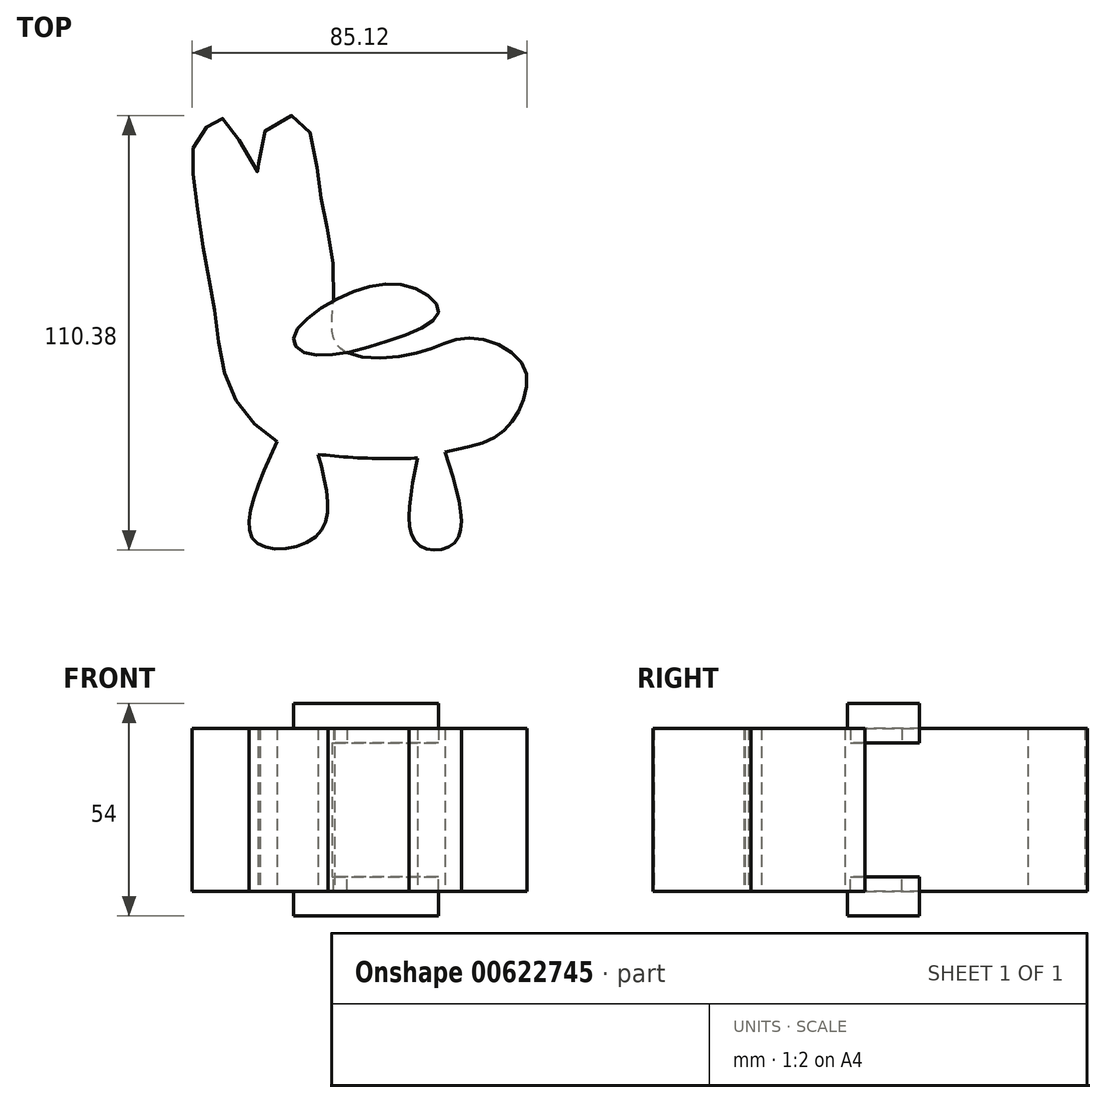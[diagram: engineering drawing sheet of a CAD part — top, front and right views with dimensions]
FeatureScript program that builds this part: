
annotation { "Feature Type Name" : "Feature", "Feature Type Description" : "" }
export const myFeature = defineFeature(function(context is Context, id is Id, definition is map)
    precondition{}
    {
        {
            var Q0;
            Q0=qCreatedBy(makeId("Top.planeOp"),FACE);
            var sketch = newSketch(context, id + "F0", { "sketchPlane" : qUnion([Q0])});
            skFitSpline(sketch, "E0", {"points": [v(13.16, -18.78) * mm, v(0, -22.63) * mm, v(-19.97, -21.15) * mm, v(-21.15, -6.36) * mm, v(-23.52, 11.68) * mm, v(-25.59, 24.4) * mm, v(-30.32, 37.42) * mm, v(-40.08, 31.2) * mm, v(-40.08, 22.63) * mm, v(-47.77, 35.35) * mm, v(-50.73, 36.83) * mm, v(-56.35, 31.2) * mm, v(-56.94, 22.04) * mm, v(-54.28, 2.81) * mm, v(-51.62, -11.1) * mm, v(-49.55, -25.59) * mm, v(-44.52, -37.12) * mm, v(-35.64, -45.1) * mm, v(-25.3, -48.36) * mm, v(0, -49.25) * mm, v(6.95, -47.77) * mm, v(18.78, -44.52) * mm, v(25.88, -36.83) * mm, v(26.77, -25.59) * mm, v(13.16, -18.78) * mm]});
            skFitSpline(sketch, "E1", {"points": [v(-35.64, -45.1) * mm, v(-41.26, -70.55) * mm, v(-25.3, -68.77) * mm, v(-25.3, -48.36) * mm], "startDerivative": vector(-39.25, -85.92) * mm, "endDerivative": vector(-19.43, 72.55) * mm});
            skFitSpline(sketch, "E2", {"points": [v(0, -49.25) * mm, v(0, -71.14) * mm, v(9.61, -70.55) * mm, v(6.95, -47.77) * mm], "startDerivative": vector(-15, -74.43) * mm, "endDerivative": vector(-23.94, 74.06) * mm});
            skSolve(sketch);
        }
        {
            var Q0;
            Q0 = qSketchRegion(id + "F0", true);
            extrude(context, id + "F1", {"entities" : qUnion([Q0]), "depth" : 37.7 * mm, "offsetDistance" : 25 * mm});
        }
        {
            var Q0;
            Q0=qCreatedBy(makeId("Top.planeOp"),FACE);
            cPlane(context, id + "F2", {"entities" : qUnion([Q0]), "cplaneType" : CPlaneType.OFFSET, "offset" : 17 * mm, "width" : 150 * mm, "height" : 150 * mm});
        }
        {
            var Q0;
            Q0=qCreatedBy(makeId("Top.planeOp"),FACE);
            var sketch = newSketch(context, id + "F3", { "sketchPlane" : qUnion([Q0])});
            skFitSpline(sketch, "E3", {"points": [v(-31.55, -18.93) * mm, v(-20.08, -8.7) * mm, v(-2.28, -5.63) * mm, v(5.31, -12) * mm, v(-5.6, -18.94) * mm, v(-27.22, -22.96) * mm, v(-31.55, -18.93) * mm]});
            skSolve(sketch);
        }
        {
            var Q0;
            Q0=makeQuery(id+"F3.imprint","IMPRINT",FACE,{"disambiguationData":[TD([[makeQuery(id+"F3.imprint","IMPRINT",EDGE,{"derivedFrom":sQuery(id+"F3.wireOp",EDGE,"E3")}),-1.0]])]});
            extrude(context, id + "F4", {"entities" : qUnion([Q0]), "operationType" : NewBodyOperationType.ADD, "oppositeDirection" : true, "depth" : 10 * mm, "offsetDistance" : 25 * mm});
        }
        {
            var Q0;
            Q0=makeQuery(id+"F1.opExtrude","SWEPT_BODY",BODY,{"disambiguationData":[OSD([sQuery(id+"F0.wireOp",EDGE,"E0"),sQuery(id+"F0.wireOp",EDGE,"E1"),sQuery(id+"F0.wireOp",EDGE,"E2")])]});
            var Q1;
            Q1=qCreatedBy(id+"F2.planeOp",FACE);
            mirror(context, id + "F5", {"operationType" : NewBodyOperationType.ADD, "entities" : qUnion([Q0]), "mirrorPlane" : qUnion([Q1])});
        }
    });
